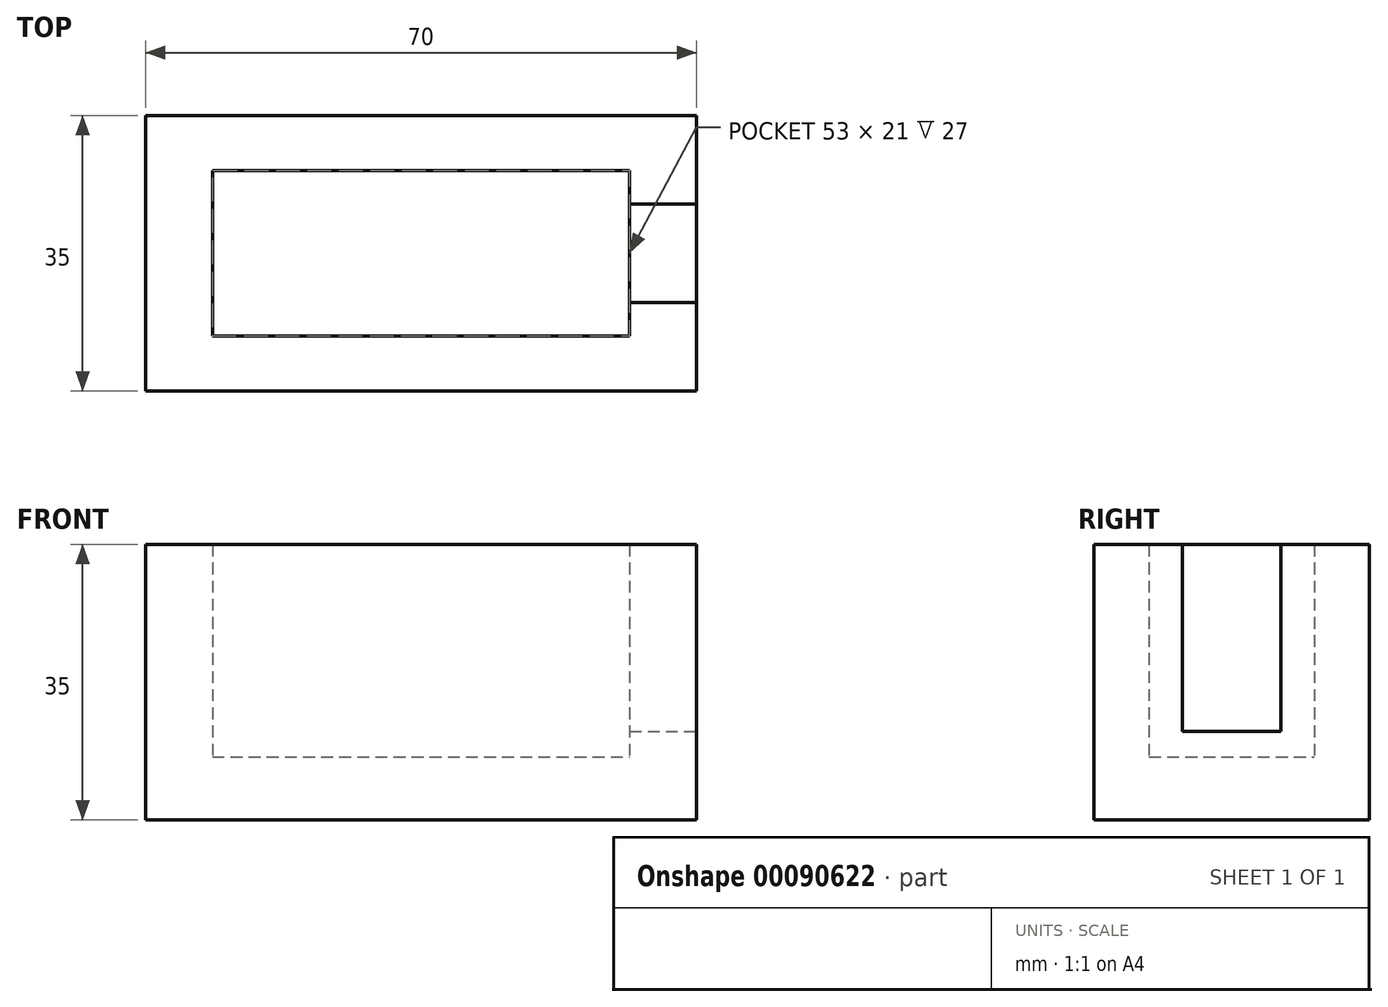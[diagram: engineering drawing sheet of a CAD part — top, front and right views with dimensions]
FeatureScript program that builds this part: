
annotation { "Feature Type Name" : "Feature", "Feature Type Description" : "" }
export const myFeature = defineFeature(function(context is Context, id is Id, definition is map)
    precondition{}
    {
        {
            var Q0;
            Q0=qCreatedBy(makeId("Top.planeOp"),FACE);
            var sketch = newSketch(context, id + "F0", { "sketchPlane" : qUnion([Q0])});
            skLineSegment(sketch, "E0.bottom", {"start": v(35, 17.5) * mm, "end": v(-35, 17.5) * mm});
            skLineSegment(sketch, "E0.top", {"start": v(35, -17.5) * mm, "end": v(-35, -17.5) * mm});
            skLineSegment(sketch, "E0.left", {"start": v(35, 17.5) * mm, "end": v(35, -17.5) * mm});
            skLineSegment(sketch, "E0.right", {"start": v(-35, 17.5) * mm, "end": v(-35, -17.5) * mm});
            skPoint(sketch, "E0.middle", {"position": v(0, 0) * mm});
            skSolve(sketch);
        }
        {
            var Q0;
            Q0=makeQuery(id+"F0.imprint","IMPRINT",FACE,{"disambiguationData":[TD([[makeQuery(id+"F0.imprint","IMPRINT",EDGE,{"derivedFrom":sQuery(id+"F0.wireOp",EDGE,"E0.bottom")}),1.0]])]});
            extrude(context, id + "F1", {"entities" : qUnion([Q0]), "depth" : 35 * mm});
        }
        {
            var Q0;
            Q0=qCreatedBy(makeId("Right.planeOp"),FACE);
            var sketch = newSketch(context, id + "F2", { "sketchPlane" : qUnion([Q0])});
            skLineSegment(sketch, "E1.bottom", {"start": v(-10.5, 27) * mm, "end": v(10.5, 27) * mm});
            skLineSegment(sketch, "E1.top", {"start": v(-10.5, 8) * mm, "end": v(10.5, 8) * mm});
            skLineSegment(sketch, "E1.left", {"start": v(-10.5, 27) * mm, "end": v(-10.5, 8) * mm});
            skLineSegment(sketch, "E1.right", {"start": v(10.5, 27) * mm, "end": v(10.5, 8) * mm});
            skPoint(sketch, "E1.middle", {"position": v(0, 17.5) * mm});
            skPoint(sketch, "E2", {"position": v(-17.5, 17.5) * mm});
            skSolve(sketch);
        }
        {
            var Q0;
            Q0 = qSketchRegion(id + "F2", true);
            extrude(context, id + "F3", {"entities" : qUnion([Q0]), "operationType" : NewBodyOperationType.REMOVE, "endBound" : BoundingType.SYMMETRIC, "oppositeDirection" : true, "depth" : 53 * mm});
        }
        {
            var Q0;
            Q0=makeQuery(id+"F1.opExtrude","SWEPT_FACE",FACE,{"disambiguationData":[OSD([sQuery(id+"F0.wireOp",EDGE,"E0.left")])]});
            var sketch = newSketch(context, id + "F4", { "sketchPlane" : qUnion([Q0])});
            skLineSegment(sketch, "E3.bottom", {"start": v(6.25, 23.75) * mm, "end": v(-6.25, 23.75) * mm});
            skLineSegment(sketch, "E3.top", {"start": v(6.25, 11.25) * mm, "end": v(-6.25, 11.25) * mm});
            skLineSegment(sketch, "E3.left", {"start": v(6.25, 23.75) * mm, "end": v(6.25, 11.25) * mm});
            skLineSegment(sketch, "E3.right", {"start": v(-6.25, 23.75) * mm, "end": v(-6.25, 11.25) * mm});
            skPoint(sketch, "E3.middle", {"position": v(0, 17.5) * mm});
            skPoint(sketch, "E4", {"position": v(17.5, 17.5) * mm});
            skSolve(sketch);
        }
        {
            var Q0;
            Q0=makeQuery(id+"F4.imprint","IMPRINT",FACE,{"disambiguationData":[TD([[makeQuery(id+"F4.imprint","IMPRINT",EDGE,{"derivedFrom":sQuery(id+"F4.wireOp",EDGE,"E3.bottom")}),1.0]])]});
            extrude(context, id + "F5", {"entities" : qUnion([Q0]), "operationType" : NewBodyOperationType.REMOVE, "oppositeDirection" : true, "depth" : 10 * mm});
        }
        {
            var Q0;
            Q0=makeQuery(id+"F1.opExtrude","CAP_FACE",FACE,{"disambiguationData":[OSD([sQuery(id+"F0.wireOp",EDGE,"E0.bottom"),sQuery(id+"F0.wireOp",EDGE,"E0.top"),sQuery(id+"F0.wireOp",EDGE,"E0.left"),sQuery(id+"F0.wireOp",EDGE,"E0.right")])],"isStart":false});
            var sketch = newSketch(context, id + "F6", { "sketchPlane" : qUnion([Q0])});
            skLineSegment(sketch, "E5", {"start": v(-26.5, 10.5) * mm, "end": v(-26.5, -10.5) * mm});
            skLineSegment(sketch, "E6", {"start": v(-26.5, -10.5) * mm, "end": v(26.5, -10.5) * mm});
            skLineSegment(sketch, "E7", {"start": v(-26.5, 10.5) * mm, "end": v(26.5, 10.5) * mm});
            skLineSegment(sketch, "E8", {"start": v(26.5, 10.5) * mm, "end": v(26.5, 6.25) * mm});
            skLineSegment(sketch, "E9", {"start": v(26.5, 6.25) * mm, "end": v(35, 6.25) * mm});
            skLineSegment(sketch, "E10", {"start": v(35, 6.25) * mm, "end": v(35, -6.25) * mm});
            skLineSegment(sketch, "E11", {"start": v(35, -6.25) * mm, "end": v(26.5, -6.25) * mm});
            skLineSegment(sketch, "E12", {"start": v(26.5, -6.25) * mm, "end": v(26.5, -10.5) * mm});
            skSolve(sketch);
        }
        {
            var Q0;
            Q0 = qSketchRegion(id + "F6", true);
            extrude(context, id + "F7", {"entities" : qUnion([Q0]), "operationType" : NewBodyOperationType.REMOVE, "oppositeDirection" : true, "depth" : 12 * mm});
        }
    });
